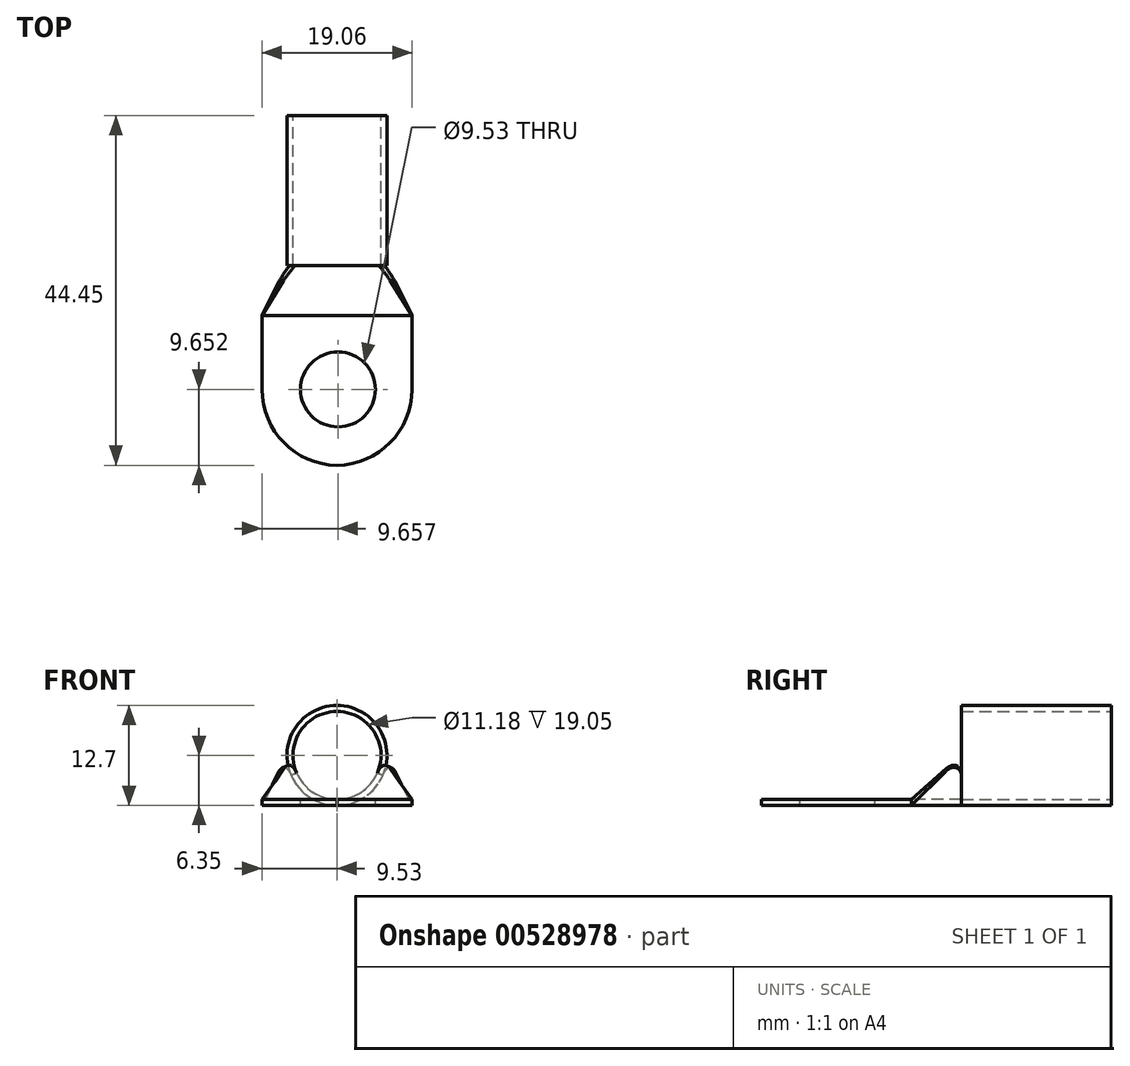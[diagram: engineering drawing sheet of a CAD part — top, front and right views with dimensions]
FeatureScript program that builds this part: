
annotation { "Feature Type Name" : "Feature", "Feature Type Description" : "" }
export const myFeature = defineFeature(function(context is Context, id is Id, definition is map)
    precondition{}
    {
        {
            var Q0;
            Q0=qCreatedBy(makeId("Front.planeOp"),FACE);
            var sketch = newSketch(context, id + "F0", { "sketchPlane" : qUnion([Q0])});
            skCircle(sketch, "E0", {"center": v(0, 0) * mm, "radius": 6.35 * mm});
            skCircle(sketch, "E1", {"center": v(0, 0) * mm, "radius": 5.59 * mm});
            skSolve(sketch);
        }
        {
            var Q0;
            Q0=qSketchRegion(id+"F0",true);
            extrude(context, id + "F1", {"entities" : qUnion([Q0]), "depth" : 19.05 * mm});
        }
        {
            var Q0;
            Q0=qCreatedBy(makeId("Front.planeOp"),FACE);
            cPlane(context, id + "F2", {"entities" : qUnion([Q0]), "cplaneType" : CPlaneType.OFFSET, "offset" : 50.8 * mm, "width" : 152.4 * mm, "height" : 152.4 * mm});
        }
        {
            var Q0;
            Q0=makeQuery(id+"F1.opExtrude","CAP_FACE",FACE,{"disambiguationData":[OSD([sQuery(id+"F0.wireOp",EDGE,"E0"),sQuery(id+"F0.wireOp",EDGE,"E1")])],"isStart":false});
            var sketch = newSketch(context, id + "F3", { "sketchPlane" : qUnion([Q0])});
            skArc(sketch, "E2.0", {"start": v(-5.59, 0) * mm, "mid": v(0, -5.59) * mm, "end": v(5.59, 0) * mm});
            skArc(sketch, "E2.1", {"start": v(-6.35, 0) * mm, "mid": v(0, -6.35) * mm, "end": v(6.35, 0) * mm});
            skLineSegment(sketch, "E3", {"start": v(-6.35, 0) * mm, "end": v(-5.59, 0) * mm});
            skLineSegment(sketch, "E4", {"start": v(5.59, 0) * mm, "end": v(6.35, 0) * mm});
            skSolve(sketch);
        }
        {
            var Q0;
            Q0=qCreatedBy(makeId("Front.planeOp"),FACE);
            cPlane(context, id + "F4", {"entities" : qUnion([Q0]), "cplaneType" : CPlaneType.OFFSET, "offset" : 25.4 * mm, "width" : 152.4 * mm, "height" : 152.4 * mm});
        }
        {
            var Q0;
            Q0=qCreatedBy(id+"F4.planeOp",FACE);
            var sketch = newSketch(context, id + "F5", { "sketchPlane" : qUnion([Q0])});
            skLineSegment(sketch, "E5.bottom", {"start": v(9.53, -5.59) * mm, "end": v(-9.53, -5.59) * mm});
            skLineSegment(sketch, "E5.top", {"start": v(9.53, -6.35) * mm, "end": v(-9.53, -6.35) * mm});
            skLineSegment(sketch, "E5.left", {"start": v(9.53, -5.59) * mm, "end": v(9.53, -6.35) * mm});
            skLineSegment(sketch, "E5.right", {"start": v(-9.53, -5.59) * mm, "end": v(-9.53, -6.35) * mm});
            skPoint(sketch, "E5.middle", {"position": v(0, -5.97) * mm});
            skSolve(sketch);
        }
        {
            var Q0;
            Q0=qSketchRegion(id+"F3",true);
            var Q1;
            Q1=qSketchRegion(id+"F5",true);
            loft(context, id + "F6", {"sheetProfilesArray" : [{ "sheetProfileEntities" : qUnion([Q0]) }, { "sheetProfileEntities" : qUnion([Q1]) }]});
        }
        {
            var Q0;
            Q0=makeQuery(id+"F6.opLoft","CAP_FACE",FACE,{"disambiguationData":[OSD([makeQuery(id+"F5.imprint","IMPRINT",FACE,{"disambiguationData":[TD([[makeQuery(id+"F5.imprint","IMPRINT",EDGE,{"derivedFrom":sQuery(id+"F5.wireOp",EDGE,"E5.bottom")}),1.0]])]})])],"isStart":true});
            extrude(context, id + "F7", {"entities" : qUnion([Q0]), "operationType" : NewBodyOperationType.ADD, "depth" : 19.05 * mm});
        }
        {
            var Q0;
            Q0=makeQuery(id+"F7.opExtrude","CAP_EDGE",EDGE,{"disambiguationData":[OSD([sQuery(id+"F5.wireOp",EDGE,"E5.bottom"),sQuery(id+"F5.wireOp",EDGE,"E5.top"),sQuery(id+"F5.wireOp",EDGE,"E5.left")])],"isStart":false});
            var Q1;
            Q1=makeQuery(id+"F7.opExtrude","CAP_EDGE",EDGE,{"disambiguationData":[OSD([sQuery(id+"F5.wireOp",EDGE,"E5.bottom"),sQuery(id+"F5.wireOp",EDGE,"E5.top"),sQuery(id+"F5.wireOp",EDGE,"E5.right")])],"isStart":false});
            fillet(context, id + "F8", {"entities" : qUnion([Q0, Q1]), "radius" : 9.65 * mm, "tangentPropagation" : true, "allowEdgeOverflow" : false});
        }
        {
            var Q0;
            Q0=makeQuery(id+"F6.opLoft","MID_CAP_EDGE",EDGE,{"disambiguationData":[OSD([sQuery(id+"F0.wireOp",EDGE,"E0"),sQuery(id+"F0.wireOp",EDGE,"E1"),sQuery(id+"F3.wireOp",EDGE,"E2.0"),sQuery(id+"F3.wireOp",EDGE,"E2.1"),sQuery(id+"F3.wireOp",EDGE,"E4")])],"capPos":0.0});
            var Q1;
            Q1=makeQuery(id+"F6.opLoft","MID_CAP_EDGE",EDGE,{"disambiguationData":[OSD([sQuery(id+"F0.wireOp",EDGE,"E0"),sQuery(id+"F0.wireOp",EDGE,"E1"),sQuery(id+"F3.wireOp",EDGE,"E2.0"),sQuery(id+"F3.wireOp",EDGE,"E2.1"),sQuery(id+"F3.wireOp",EDGE,"E3")])],"capPos":0.0});
            fillet(context, id + "F9", {"entities" : qUnion([Q0, Q1]), "radius" : 1.27 * mm, "tangentPropagation" : true, "allowEdgeOverflow" : false});
        }
        {
            var Q0;
            Q0=makeQuery(id+"F7.opExtrude","SWEPT_FACE",FACE,{"disambiguationData":[OSD([sQuery(id+"F5.wireOp",EDGE,"E5.bottom"),sQuery(id+"F5.wireOp",EDGE,"E5.left"),sQuery(id+"F5.wireOp",EDGE,"E5.right")])]});
            var sketch = newSketch(context, id + "F10", { "sketchPlane" : qUnion([Q0])});
            skCircle(sketch, "E6", {"center": v(0.13, -34.8) * mm, "radius": 4.76 * mm});
            skSolve(sketch);
        }
        {
            var Q0;
            Q0=qSketchRegion(id+"F10",true);
            extrude(context, id + "F11", {"entities" : qUnion([Q0]), "operationType" : NewBodyOperationType.REMOVE, "oppositeDirection" : true, "depth" : 25.4 * mm});
        }
    });
